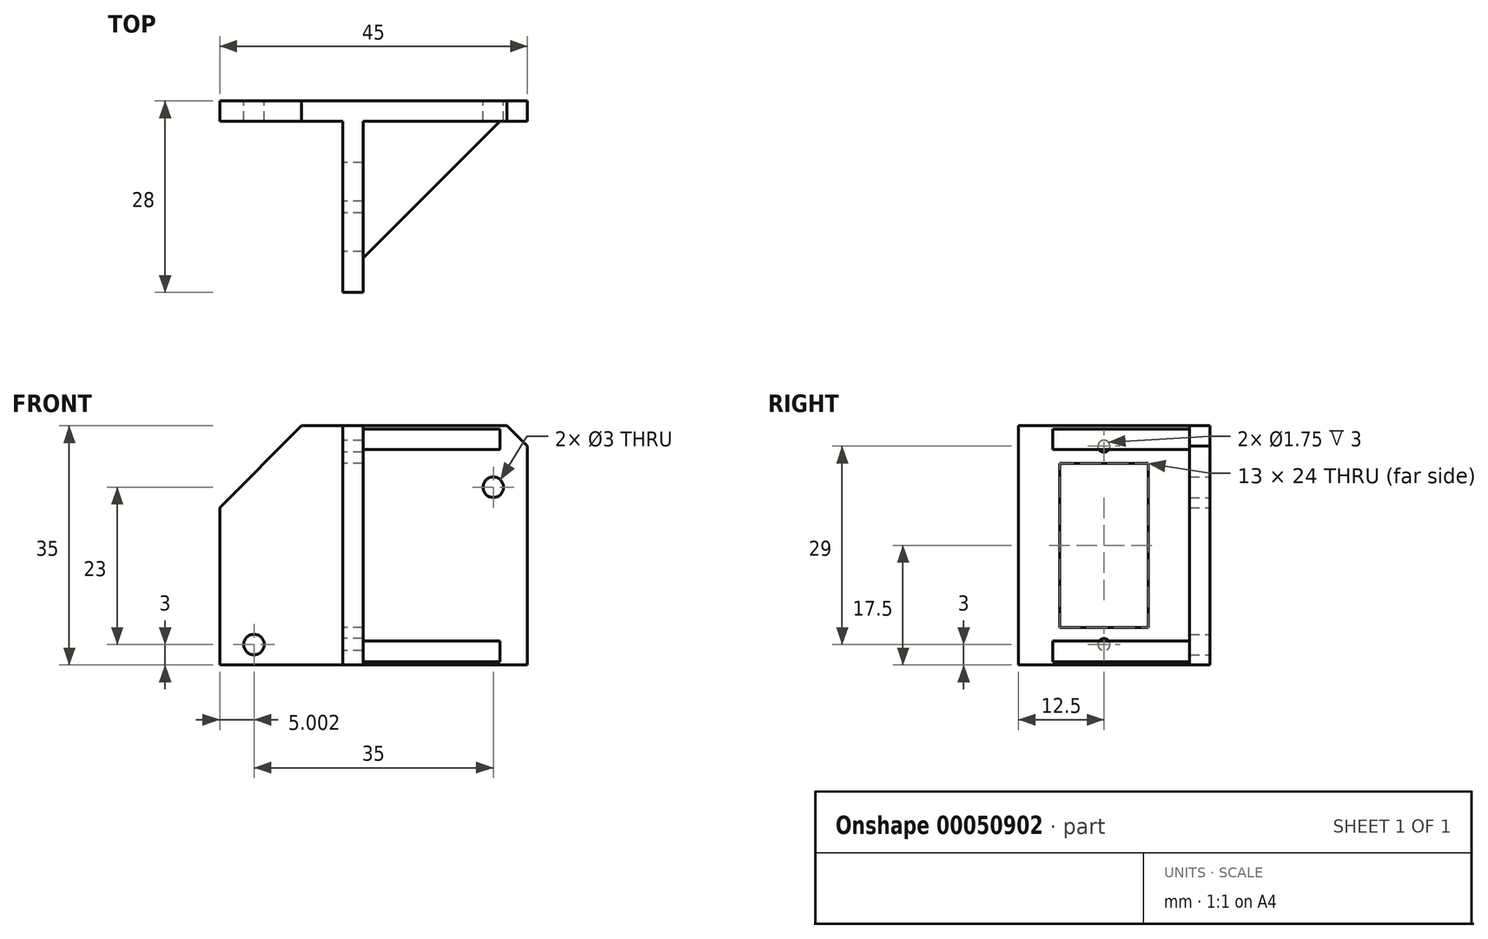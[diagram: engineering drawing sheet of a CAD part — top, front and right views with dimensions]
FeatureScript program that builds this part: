
annotation { "Feature Type Name" : "Feature", "Feature Type Description" : "" }
export const myFeature = defineFeature(function(context is Context, id is Id, definition is map)
    precondition{}
    {
        {
            var Q0;
            Q0=qCreatedBy(makeId("Front.planeOp"),FACE);
            var sketch = newSketch(context, id + "F0", { "sketchPlane" : qUnion([Q0])});
            skLineSegment(sketch, "E0", {"start": v(-19.1, 0) * mm, "end": v(25.9, 0) * mm});
            skLineSegment(sketch, "E1", {"start": v(25.9, 0) * mm, "end": v(25.9, 32) * mm});
            skLineSegment(sketch, "E2", {"start": v(25.9, 32) * mm, "end": v(22.9, 35) * mm});
            skLineSegment(sketch, "E3", {"start": v(22.9, 35) * mm, "end": v(-7.14, 35) * mm});
            skLineSegment(sketch, "E4", {"start": v(-7.14, 35) * mm, "end": v(-19.1, 23.03) * mm});
            skLineSegment(sketch, "E5", {"start": v(-19.1, 23.03) * mm, "end": v(-19.1, 0) * mm});
            skCircle(sketch, "E6", {"center": v(20.9, 26) * mm, "radius": 1.5 * mm});
            skCircle(sketch, "E7", {"center": v(-14.1, 3) * mm, "radius": 1.5 * mm});
            skSolve(sketch);
        }
        {
            var Q0;
            Q0=makeQuery(id+"F0.imprint","IMPRINT",FACE,{"disambiguationData":[TD([[makeQuery(id+"F0.imprint","IMPRINT",EDGE,{"derivedFrom":sQuery(id+"F0.wireOp",EDGE,"E0")}),1.0]])]});
            extrude(context, id + "F1", {"entities" : qUnion([Q0]), "depth" : 3 * mm});
        }
        {
            var Q0;
            Q0=makeQuery(id+"F1.opExtrude","CAP_FACE",FACE,{"disambiguationData":[OSD([sQuery(id+"F0.wireOp",EDGE,"E0"),sQuery(id+"F0.wireOp",EDGE,"E1"),sQuery(id+"F0.wireOp",EDGE,"E2"),sQuery(id+"F0.wireOp",EDGE,"E3"),sQuery(id+"F0.wireOp",EDGE,"E4"),sQuery(id+"F0.wireOp",EDGE,"E5"),sQuery(id+"F0.wireOp",EDGE,"E6"),sQuery(id+"F0.wireOp",EDGE,"E7")])],"isStart":false});
            var sketch = newSketch(context, id + "F2", { "sketchPlane" : qUnion([Q0])});
            skLineSegment(sketch, "E8", {"start": v(-1.1, 0) * mm, "end": v(-1.1, 35) * mm});
            skLineSegment(sketch, "E9", {"start": v(-1.1, 35) * mm, "end": v(1.9, 35) * mm});
            skLineSegment(sketch, "E10", {"start": v(1.9, 35) * mm, "end": v(1.9, 0) * mm});
            skLineSegment(sketch, "E11", {"start": v(1.9, 0) * mm, "end": v(-1.1, 0) * mm});
            skSolve(sketch);
        }
        {
            var Q0;
            Q0=makeQuery(id+"F2.imprint","IMPRINT",FACE,{"disambiguationData":[TD([[makeQuery(id+"F2.imprint","IMPRINT",EDGE,{"derivedFrom":sQuery(id+"F2.wireOp",EDGE,"E8")}),-1.0]])]});
            extrude(context, id + "F3", {"entities" : qUnion([Q0]), "operationType" : NewBodyOperationType.ADD, "depth" : 25 * mm});
        }
        {
            var Q0;
            Q0=makeQuery(id+"F3.opExtrude","SWEPT_FACE",FACE,{"disambiguationData":[OSD([sQuery(id+"F2.wireOp",EDGE,"E8")])]});
            var sketch = newSketch(context, id + "F4", { "sketchPlane" : qUnion([Q0])});
            skLineSegment(sketch, "E12.rect.bottom", {"start": v(22, 29.5) * mm, "end": v(9, 29.5) * mm});
            skLineSegment(sketch, "E12.rect.top", {"start": v(22, 5.5) * mm, "end": v(9, 5.5) * mm});
            skLineSegment(sketch, "E12.rect.left", {"start": v(22, 29.5) * mm, "end": v(22, 5.5) * mm});
            skLineSegment(sketch, "E12.rect.right", {"start": v(9, 29.5) * mm, "end": v(9, 5.5) * mm});
            skPoint(sketch, "E12.rect.middle", {"position": v(15.5, 17.5) * mm});
            skPoint(sketch, "E12.rect.middle.positionSnap0", {"position": v(15.5, 35) * mm});
            skPoint(sketch, "E12.rect.middle.positionSnap1", {"position": v(28, 17.5) * mm});
            skPoint(sketch, "E12.rect.centerSnap0", {"position": v(15.5, 35) * mm});
            skPoint(sketch, "E12.rect.centerSnap1", {"position": v(28, 17.5) * mm});
            skCircle(sketch, "E13", {"center": v(15.5, 32) * mm, "radius": 0.88 * mm});
            skCircle(sketch, "E14", {"center": v(15.5, 3) * mm, "radius": 0.88 * mm});
            skPoint(sketch, "E14.centerSnap0", {"position": v(15.5, 5.5) * mm});
            skSolve(sketch);
        }
        {
            var Q0;
            Q0=makeQuery(id+"F4.imprint","IMPRINT",FACE,{"disambiguationData":[TD([[makeQuery(id+"F4.imprint","IMPRINT",EDGE,{"derivedFrom":sQuery(id+"F4.wireOp",EDGE,"E12.rect.bottom")}),1.0]])]});
            var Q1;
            Q1=makeQuery(id+"F4.imprint","IMPRINT",FACE,{"disambiguationData":[TD([[makeQuery(id+"F4.imprint","IMPRINT",EDGE,{"derivedFrom":sQuery(id+"F4.wireOp",EDGE,"E13")}),1.0]])]});
            var Q2;
            Q2=makeQuery(id+"F4.imprint","IMPRINT",FACE,{"disambiguationData":[TD([[makeQuery(id+"F4.imprint","IMPRINT",EDGE,{"derivedFrom":sQuery(id+"F4.wireOp",EDGE,"E14")}),1.0]])]});
            extrude(context, id + "F5", {"entities" : qUnion([Q0, Q1, Q2]), "operationType" : NewBodyOperationType.REMOVE, "endBound" : BoundingType.THROUGH_ALL, "oppositeDirection" : true, "depth" : 25 * mm});
        }
        {
            var Q0;
            {var subQ0=sQuery(id+"F0.wireOp",EDGE,"E3");var subQ1=sQuery(id+"F0.wireOp",EDGE,"E2");var subQ2=sQuery(id+"F0.wireOp",EDGE,"E1");var subQ3=sQuery(id+"F0.wireOp",EDGE,"E0");var subQ4=sQuery(id+"F0.wireOp",EDGE,"E6");Q0=makeQuery(id+"F3.boolean.opBoolean","SPLIT",FACE,{"disambiguationData":[TD([makeQuery(id+"F1.opExtrude","SWEPT_FACE",FACE,{"disambiguationData":[OSD([subQ2])]})])],"derivedFrom":makeQuery(id+"F1.opExtrude","CAP_FACE",FACE,{"disambiguationData":[OSD([subQ3,subQ2,subQ1,subQ0,sQuery(id+"F0.wireOp",EDGE,"E4"),sQuery(id+"F0.wireOp",EDGE,"E5"),subQ4,sQuery(id+"F0.wireOp",EDGE,"E7")])],"isStart":false})});}
            var sketch = newSketch(context, id + "F6", { "sketchPlane" : qUnion([Q0])});
            skLineSegment(sketch, "E15", {"start": v(1.9, 31.5) * mm, "end": v(21.9, 31.5) * mm});
            skLineSegment(sketch, "E16", {"start": v(21.9, 31.5) * mm, "end": v(21.9, 34.5) * mm});
            skLineSegment(sketch, "E17", {"start": v(21.9, 34.5) * mm, "end": v(1.9, 34.5) * mm});
            skLineSegment(sketch, "E18", {"start": v(1.9, 34.5) * mm, "end": v(1.9, 31.5) * mm});
            skLineSegment(sketch, "E19", {"start": v(1.9, 3.5) * mm, "end": v(21.9, 3.5) * mm});
            skLineSegment(sketch, "E20", {"start": v(21.9, 3.5) * mm, "end": v(21.9, 0.5) * mm});
            skLineSegment(sketch, "E21", {"start": v(21.9, 0.5) * mm, "end": v(1.9, 0.5) * mm});
            skLineSegment(sketch, "E22", {"start": v(1.9, 0.5) * mm, "end": v(1.9, 3.5) * mm});
            skSolve(sketch);
        }
        {
            var Q0;
            Q0 = qSketchRegion(id + "F6", true);
            extrude(context, id + "F7", {"entities" : qUnion([Q0]), "operationType" : NewBodyOperationType.ADD, "depth" : 23 * mm});
        }
        {
            var Q0;
            Q0=makeQuery(id+"F7.opExtrude","CAP_EDGE",EDGE,{"disambiguationData":[OSD([sQuery(id+"F6.wireOp",EDGE,"E20")])],"isStart":false});
            chamfer(context, id + "F8", {"entities" : qUnion([Q0]), "chamferType" : ChamferType.OFFSET_ANGLE, "width" : 23 * mm, "oppositeDirection" : false, "angle" : 45 * degree, "tangentPropagation" : true});
        }
        {
            var Q0;
            Q0=makeQuery(id+"F7.opExtrude","CAP_EDGE",EDGE,{"disambiguationData":[OSD([sQuery(id+"F6.wireOp",EDGE,"E16")])],"isStart":false});
            chamfer(context, id + "F9", {"entities" : qUnion([Q0]), "chamferType" : ChamferType.OFFSET_ANGLE, "width" : 23 * mm, "oppositeDirection" : true, "angle" : 45 * degree, "tangentPropagation" : true});
        }
    });
